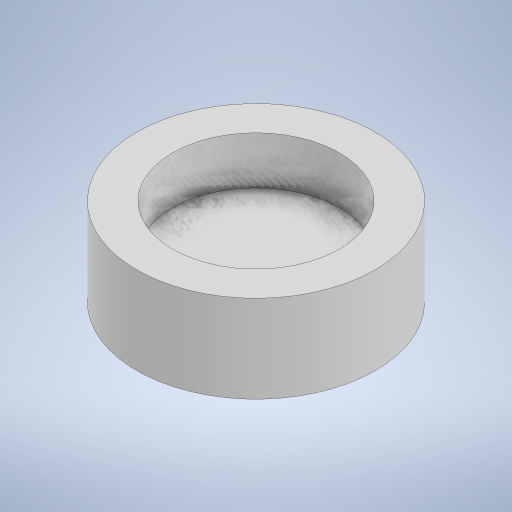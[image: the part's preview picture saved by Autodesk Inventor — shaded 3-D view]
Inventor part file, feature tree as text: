
AUTODESK INVENTOR PART (.ipt)
format: ipt  version: 2023 (Build 270158000, 158)  size: 240,640 bytes
history: native  units: mm
features: extrude x3, sketch x2, other x1, projected_geometry x1
ambient origin geometry x8: Origin, YZ Plane, XZ Plane, XY Plane, X Axis, Y Axis, Z Axis, Center Point
bodies: Body1 (feature_tree)
feature tree (7):
  other  "솔리드1"
  sketch  "스케치1"
  extrude  "돌출1"  Depth=15.0mm
  extrude  "돌출2"  Depth=10.5mm
  extrude  "돌출3"  Depth=3.0mm TaperAngle=0.0deg
  sketch  "스케치2"
  projected_geometry  "투영된 루프1"
